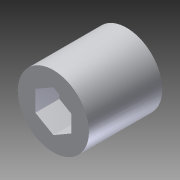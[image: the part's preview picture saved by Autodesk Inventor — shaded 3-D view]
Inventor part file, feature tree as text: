
AUTODESK INVENTOR PART (.ipt)
format: ipt  version: 2012 (Build 160160000, 160)  size: 135,168 bytes
history: native  units: in
note: dims shown in document units (in); Inventor stores cm internally (conversion verified against a paired STEP export)
features: sketch x6, extrude x6, plane x3, reference x1
ambient origin geometry x8: Origin, YZ Plane, XZ Plane, XY Plane, X Axis, Y Axis, Z Axis, Center Point
feature tree (16):
  sketch  "Sketch2"  dims[d5=0.3937in d6=0.0in d7=0.4724in d8=0.0in]
  plane  "Work Plane1"
  plane  "Work Plane2"
  plane  "Work Plane3"
  extrude  "Extrusion3"  Depth=0.4724in TaperAngle=0.0deg
  extrude  "Extrusion4"  Depth=0.0098in
  extrude  "Extrusion5"  Depth=0.0098in
  extrude  "Extrusion6"  Depth=0.0098in
  extrude  "Extrusion7"  Depth=0.0118in TaperAngle=0.0deg
  extrude  "Extrusion8"  Depth=0.1693in
  reference  "Reference1"
  sketch  "Sketch4"  dims[d9=0.0787in d10=0.0098in]
  sketch  "Sketch5"  dims[d11=0.0098in d12=0.0098in]
  sketch  "Sketch6"  dims[d13=0.0098in d14=0.0098in]
  sketch  "Sketch7"  dims[d15=0.0098in d16=0.0118in d17=0.0in]
  sketch  "Sketch10"  dims[d19=0.2756in d20=0.0in d21=0.1693in d22=0.2756in d23=0.0in d25=0.3543in d26=0.0394in d27=0.0in d32=0.0in d33=0.4764in]
